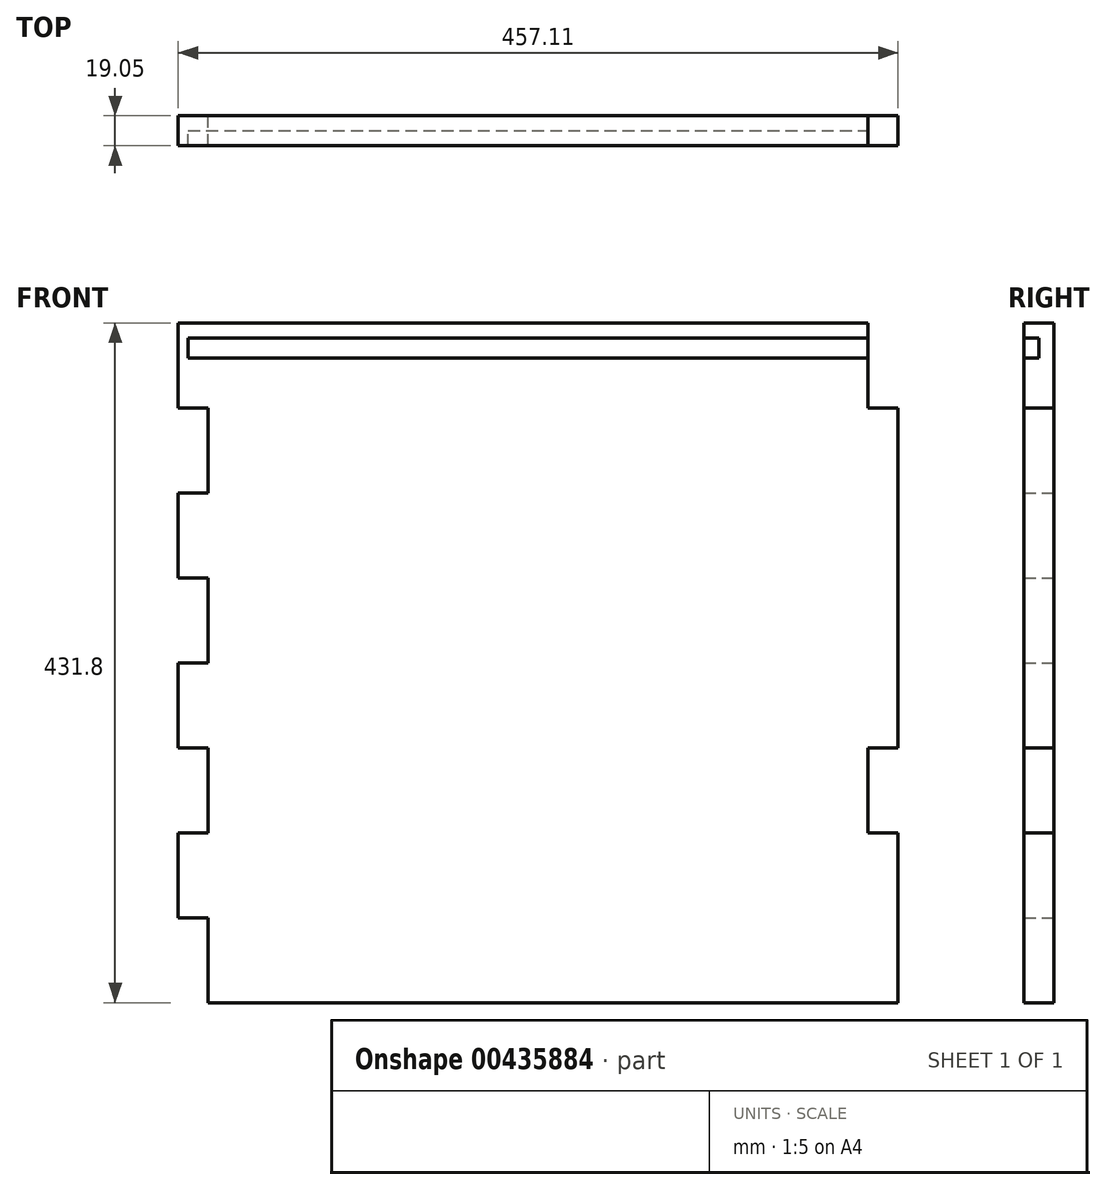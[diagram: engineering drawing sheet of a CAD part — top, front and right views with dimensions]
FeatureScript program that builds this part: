
annotation { "Feature Type Name" : "Feature", "Feature Type Description" : "" }
export const myFeature = defineFeature(function(context is Context, id is Id, definition is map)
    precondition{}
    {
        {
            var Q0;
            Q0=qCreatedBy(makeId("Front.planeOp"),FACE);
            var sketch = newSketch(context, id + "F0", { "sketchPlane" : qUnion([Q0])});
            skLineSegment(sketch, "E0.bottom", {"start": v(0, 0) * mm, "end": v(457.11, 0) * mm});
            skLineSegment(sketch, "E1", {"start": v(0, 431.8) * mm, "end": v(0, 377.83) * mm});
            skLineSegment(sketch, "E2", {"start": v(0, 377.83) * mm, "end": v(19.05, 377.83) * mm});
            skLineSegment(sketch, "E3", {"start": v(19.05, 377.83) * mm, "end": v(19.05, 323.85) * mm});
            skLineSegment(sketch, "E4", {"start": v(19.05, 323.85) * mm, "end": v(0, 323.85) * mm});
            skLineSegment(sketch, "E5", {"start": v(0, 323.85) * mm, "end": v(0, 269.88) * mm});
            skLineSegment(sketch, "E6", {"start": v(0, 269.88) * mm, "end": v(19.05, 269.88) * mm});
            skLineSegment(sketch, "E7", {"start": v(19.05, 269.88) * mm, "end": v(19.05, 215.9) * mm});
            skLineSegment(sketch, "E8", {"start": v(19.05, 215.9) * mm, "end": v(0, 215.9) * mm});
            skLineSegment(sketch, "E9", {"start": v(0, 215.9) * mm, "end": v(0, 161.93) * mm});
            skLineSegment(sketch, "E10", {"start": v(0, 161.93) * mm, "end": v(19.05, 161.93) * mm});
            skLineSegment(sketch, "E11", {"start": v(19.05, 161.93) * mm, "end": v(19.05, 107.95) * mm});
            skLineSegment(sketch, "E12", {"start": v(19.05, 107.95) * mm, "end": v(0, 107.95) * mm});
            skLineSegment(sketch, "E13", {"start": v(0, 107.95) * mm, "end": v(0, 53.98) * mm});
            skLineSegment(sketch, "E14", {"start": v(0, 53.98) * mm, "end": v(19.05, 53.98) * mm});
            skLineSegment(sketch, "E15", {"start": v(19.05, 53.98) * mm, "end": v(19.05, 0) * mm});
            skLineSegment(sketch, "E16", {"start": v(438.06, 431.8) * mm, "end": v(438.06, 377.83) * mm});
            skLineSegment(sketch, "E17", {"start": v(438.06, 377.83) * mm, "end": v(457.11, 377.83) * mm});
            skLineSegment(sketch, "E18", {"start": v(0, 431.8) * mm, "end": v(438.06, 431.8) * mm});
            skLineSegment(sketch, "E19", {"start": v(457.11, 0) * mm, "end": v(457.11, 107.95) * mm});
            skLineSegment(sketch, "E20", {"start": v(457.11, 107.95) * mm, "end": v(438.06, 107.95) * mm});
            skLineSegment(sketch, "E21", {"start": v(438.06, 107.95) * mm, "end": v(438.06, 161.93) * mm});
            skLineSegment(sketch, "E22", {"start": v(438.06, 161.93) * mm, "end": v(457.11, 161.93) * mm});
            skLineSegment(sketch, "E23", {"start": v(457.11, 161.93) * mm, "end": v(457.11, 377.83) * mm});
            skSolve(sketch);
        }
        {
            var Q0;
            Q0=makeQuery(id+"F0.imprint","IMPRINT",FACE,{"disambiguationData":[TD([[makeQuery(id+"F0.imprint","IMPRINT",EDGE,{"derivedFrom":sQuery(id+"F0.wireOp",EDGE,"E1")}),1.0]])]});
            extrude(context, id + "F1", {"entities" : qUnion([Q0]), "depth" : 19.05 * mm});
        }
        {
            var Q0;
            Q0=makeQuery(id+"F1.opExtrude","SWEPT_FACE",FACE,{"disambiguationData":[OSD([sQuery(id+"F0.wireOp",EDGE,"E16")])]});
            var sketch = newSketch(context, id + "F2", { "sketchPlane" : qUnion([Q0])});
            skLineSegment(sketch, "E24", {"start": v(-19.05, 422.27) * mm, "end": v(-9.53, 422.27) * mm});
            skLineSegment(sketch, "E25", {"start": v(-9.53, 422.27) * mm, "end": v(-9.53, 409.57) * mm});
            skLineSegment(sketch, "E26", {"start": v(-9.53, 409.57) * mm, "end": v(-19.05, 409.57) * mm});
            skSolve(sketch);
        }
        {
            var Q0;
            {var subQ0=sQuery(id+"F2.wireOp",EDGE,"E24");Q0=makeQuery(id+"F2.imprint","IMPRINT",FACE,{"disambiguationData":[TD([[makeQuery(id+"F2.imprint","IMPRINT",EDGE,{"derivedFrom":subQ0}),-1.0]])]});}
            extrude(context, id + "F3", {"entities" : qUnion([Q0]), "operationType" : NewBodyOperationType.REMOVE, "oppositeDirection" : true, "depth" : 431.8 * mm});
        }
    });
